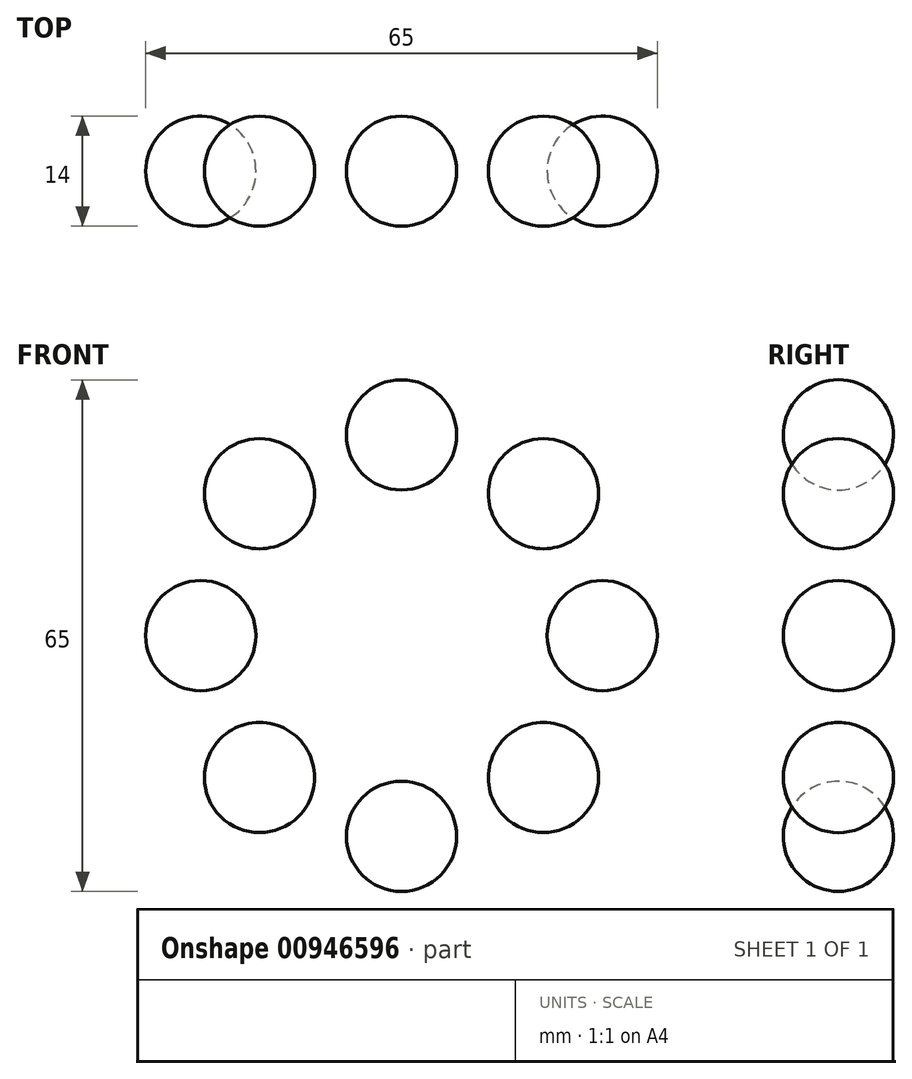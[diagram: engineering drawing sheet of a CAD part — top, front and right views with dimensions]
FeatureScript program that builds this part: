
annotation { "Feature Type Name" : "Feature", "Feature Type Description" : "" }
export const myFeature = defineFeature(function(context is Context, id is Id, definition is map)
    precondition{}
    {
        {
            var Q0;
            Q0=qCreatedBy(makeId("Front.planeOp"),FACE);
            var sketch = newSketch(context, id + "F0", { "sketchPlane" : qUnion([Q0])});
            skArc(sketch, "E0", {"start": v(7, 0) * mm, "mid": v(0, 7) * mm, "end": v(-7, 0) * mm});
            skLineSegment(sketch, "E1", {"start": v(-7, 0) * mm, "end": v(7, 0) * mm});
            skSolve(sketch);
        }
        {
            var Q0;
            Q0 = qSketchRegion(id + "F0", true);
            var Q1;
            Q1=sQuery(id+"F0.wireOp",EDGE,"E1");
            revolve(context, id + "F1", {"surfaceOperationType" : NewSurfaceOperationType.NEW, "entities" : qUnion([Q0]), "axis" : qUnion([Q1]), "revolveType" : RevolveType.FULL});
        }
        {
            var Q0;
            Q0=qCreatedBy(makeId("Front.planeOp"),FACE);
            var sketch = newSketch(context, id + "F2", { "sketchPlane" : qUnion([Q0])});
            skPoint(sketch, "E2", {"position": v(0, -25.5) * mm});
            skCircle(sketch, "E3", {"center": v(0, -25.5) * mm, "radius": 25.5 * mm, "construction": true});
            skSolve(sketch);
        }
        {
            var Q0;
            Q0=makeQuery(id+"F1.opRevolve","SWEPT_BODY",BODY,{"disambiguationData":[OSD([sQuery(id+"F0.wireOp",EDGE,"E0"),sQuery(id+"F0.wireOp",EDGE,"E1")])]});
            var Q1;
            Q1=sQuery(id+"F2.wireOp",EDGE,"E3");
            circularPattern(context, id + "F3", {"entities" : qUnion([Q0]), "axis" : qUnion([Q1]), "angle" : 360 * degree, "instanceCount" : 8, "equalSpace" : true, "computeTransformsWithoutBuiltin" : true});
        }
    });
